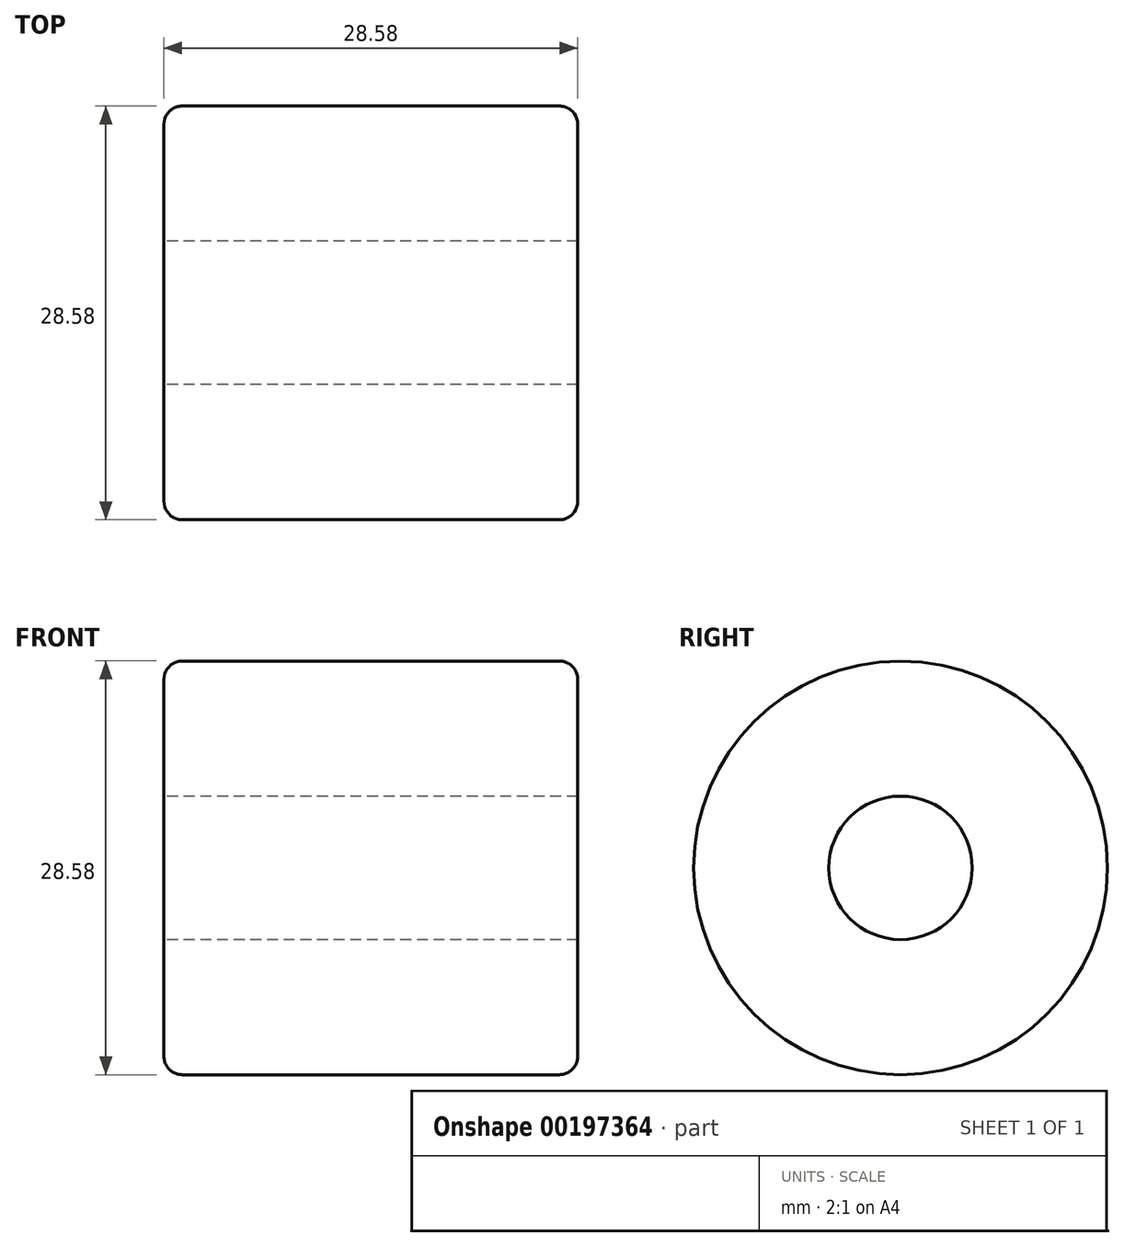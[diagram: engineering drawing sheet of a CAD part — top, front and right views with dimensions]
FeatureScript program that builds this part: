
annotation { "Feature Type Name" : "Feature", "Feature Type Description" : "" }
export const myFeature = defineFeature(function(context is Context, id is Id, definition is map)
    precondition{}
    {
        {
            var Q0;
            Q0=qCreatedBy(makeId("Right.planeOp"),FACE);
            var sketch = newSketch(context, id + "F0", { "sketchPlane" : qUnion([Q0])});
            skCircle(sketch, "E0", {"center": v(0, 0) * mm, "radius": 14.29 * mm});
            skCircle(sketch, "E1", {"center": v(0, 0) * mm, "radius": 4.95 * mm});
            skSolve(sketch);
        }
        {
            var Q0;
            Q0=qSketchRegion(id+"F0",true);
            extrude(context, id + "F1", {"entities" : qUnion([Q0]), "endBound" : BoundingType.SYMMETRIC, "depth" : 28.57 * mm});
        }
        {
            var Q0;
            Q0=makeQuery(id+"F1.opExtrude","CAP_EDGE",EDGE,{"disambiguationData":[OSD([sQuery(id+"F0.wireOp",EDGE,"E0")])],"isStart":false});
            var Q1;
            Q1=makeQuery(id+"F1.opExtrude","CAP_EDGE",EDGE,{"disambiguationData":[OSD([sQuery(id+"F0.wireOp",EDGE,"E0")])],"isStart":true});
            fillet(context, id + "F2", {"entities" : qUnion([Q0, Q1]), "radius" : 1.27 * mm, "tangentPropagation" : true, "allowEdgeOverflow" : false});
        }
    });
